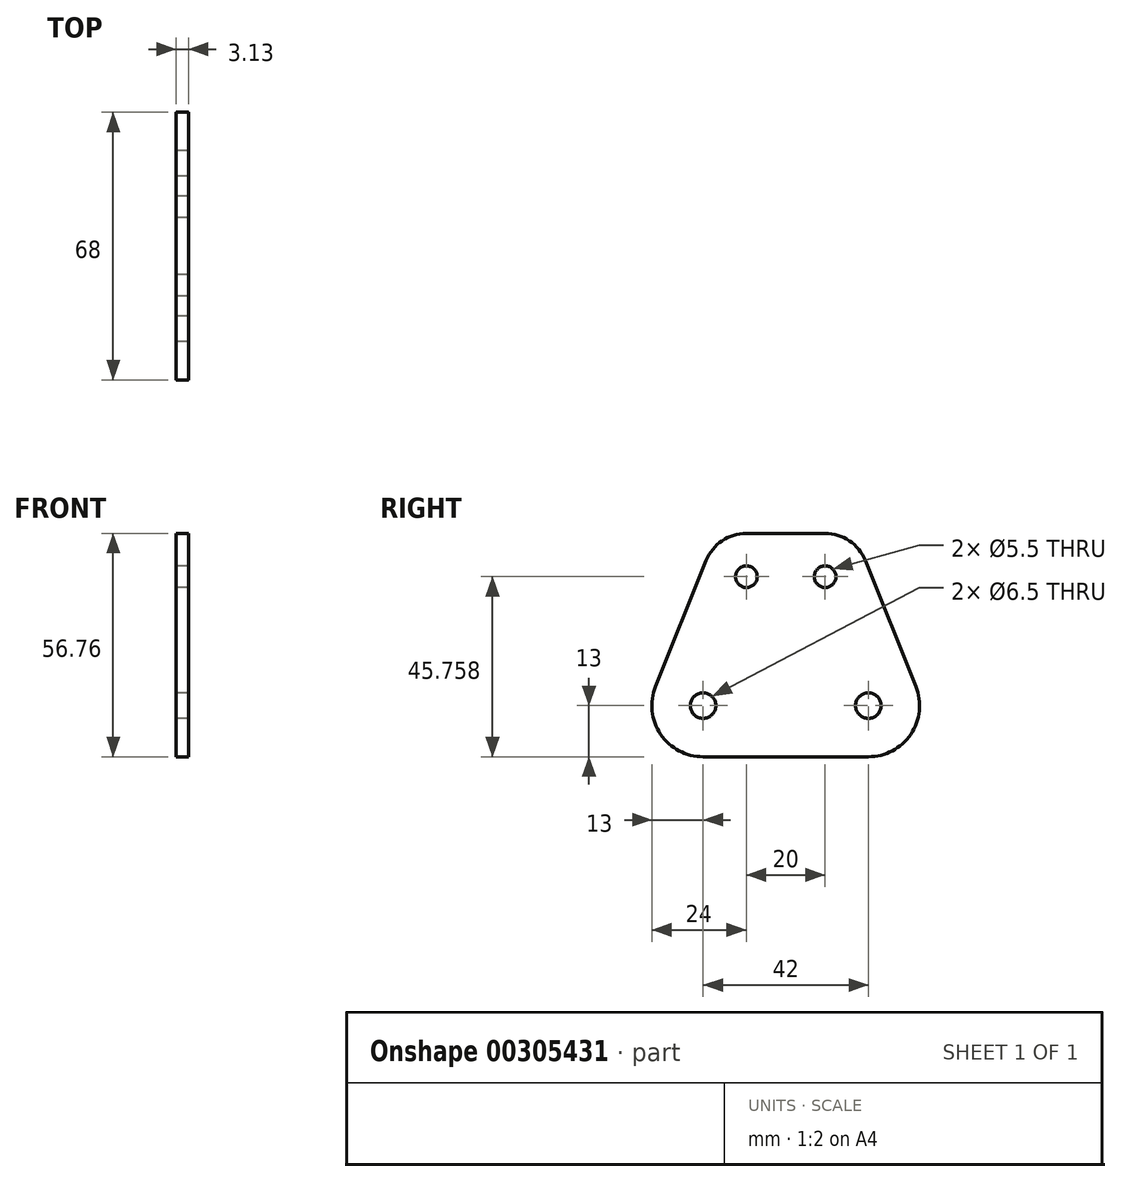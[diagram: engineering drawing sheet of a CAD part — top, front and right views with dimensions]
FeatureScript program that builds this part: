
annotation { "Feature Type Name" : "Feature", "Feature Type Description" : "" }
export const myFeature = defineFeature(function(context is Context, id is Id, definition is map)
    precondition{}
    {
        {
            var Q0;
            Q0=qCreatedBy(makeId("Right.planeOp"),FACE);
            var sketch = newSketch(context, id + "F0", { "sketchPlane" : qUnion([Q0])});
            skCircle(sketch, "E0", {"center": v(0, 0) * mm, "radius": 15 * mm});
            skCircle(sketch, "E1", {"center": v(0, 0) * mm, "radius": 27 * mm});
            skCircle(sketch, "E2", {"center": v(-21, 0) * mm, "radius": 3.25 * mm});
            skCircle(sketch, "E3", {"center": v(21, 0) * mm, "radius": 3.25 * mm});
            skCircle(sketch, "E4", {"center": v(-21, 0) * mm, "radius": 5 * mm});
            skCircle(sketch, "E5", {"center": v(21, 0) * mm, "radius": 5 * mm});
            skLineSegment(sketch, "E6.bottom", {"start": v(-20, 42.76) * mm, "end": v(20, 42.76) * mm});
            skLineSegment(sketch, "E6.top", {"start": v(-20, 22.76) * mm, "end": v(20, 22.76) * mm});
            skLineSegment(sketch, "E6.left", {"start": v(-20, 42.76) * mm, "end": v(-20, 22.76) * mm});
            skLineSegment(sketch, "E6.right", {"start": v(20, 42.76) * mm, "end": v(20, 22.76) * mm});
            skCircle(sketch, "E7", {"center": v(-10, 32.76) * mm, "radius": 4.25 * mm});
            skCircle(sketch, "E8", {"center": v(10, 32.76) * mm, "radius": 4.25 * mm});
            skPoint(sketch, "E9", {"position": v(-20, 32.76) * mm});
            skPoint(sketch, "E10", {"position": v(20, 32.76) * mm});
            skCircle(sketch, "E11", {"center": v(-10, 32.76) * mm, "radius": 2.75 * mm});
            skCircle(sketch, "E12", {"center": v(10, 32.76) * mm, "radius": 2.75 * mm});
            skPoint(sketch, "E13", {"position": v(0, 22.76) * mm});
            skSolve(sketch);
        }
        {
            var Q0;
            Q0=qCreatedBy(makeId("Right.planeOp"),FACE);
            var sketch = newSketch(context, id + "F1", { "sketchPlane" : qUnion([Q0])});
            skPoint(sketch, "E14.0", {"position": v(-10, 32.76) * mm});
            skPoint(sketch, "E15.0", {"position": v(10, 32.76) * mm});
            skPoint(sketch, "E16.0", {"position": v(-21, 0) * mm});
            skPoint(sketch, "E17.0", {"position": v(21, 0) * mm});
            skCircle(sketch, "E18", {"center": v(-21, 0) * mm, "radius": 3.25 * mm});
            skCircle(sketch, "E19", {"center": v(21, 0) * mm, "radius": 3.25 * mm});
            skCircle(sketch, "E20", {"center": v(10, 32.76) * mm, "radius": 2.75 * mm});
            skCircle(sketch, "E21", {"center": v(-10, 32.76) * mm, "radius": 2.75 * mm});
            skArc(sketch, "E22", {"start": v(-10, 43.76) * mm, "mid": v(-16.16, 41.87) * mm, "end": v(-20.2, 36.86) * mm});
            skArc(sketch, "E23", {"start": v(20.2, 36.86) * mm, "mid": v(16.16, 41.87) * mm, "end": v(10, 43.76) * mm});
            skArc(sketch, "E24", {"start": v(21, -13) * mm, "mid": v(31.77, -7.28) * mm, "end": v(33.06, 4.84) * mm});
            skArc(sketch, "E25", {"start": v(-33.06, 4.84) * mm, "mid": v(-31.77, -7.28) * mm, "end": v(-21, -13) * mm});
            skLineSegment(sketch, "E26", {"start": v(-33.06, 4.84) * mm, "end": v(-20.2, 36.86) * mm});
            skLineSegment(sketch, "E27", {"start": v(-10, 43.76) * mm, "end": v(10, 43.76) * mm});
            skLineSegment(sketch, "E28", {"start": v(20.2, 36.86) * mm, "end": v(33.06, 4.84) * mm});
            skLineSegment(sketch, "E29", {"start": v(21, -13) * mm, "end": v(-21, -13) * mm});
            skSolve(sketch);
        }
        {
            var Q0;
            Q0=makeQuery(id+"F1.imprint","IMPRINT",FACE,{"disambiguationData":[TD([[makeQuery(id+"F1.imprint","IMPRINT",EDGE,{"derivedFrom":sQuery(id+"F1.wireOp",EDGE,"E18")}),-1.0]])]});
            extrude(context, id + "F2", {"entities" : qUnion([Q0]), "depth" : 3.12 * mm});
        }
    });
